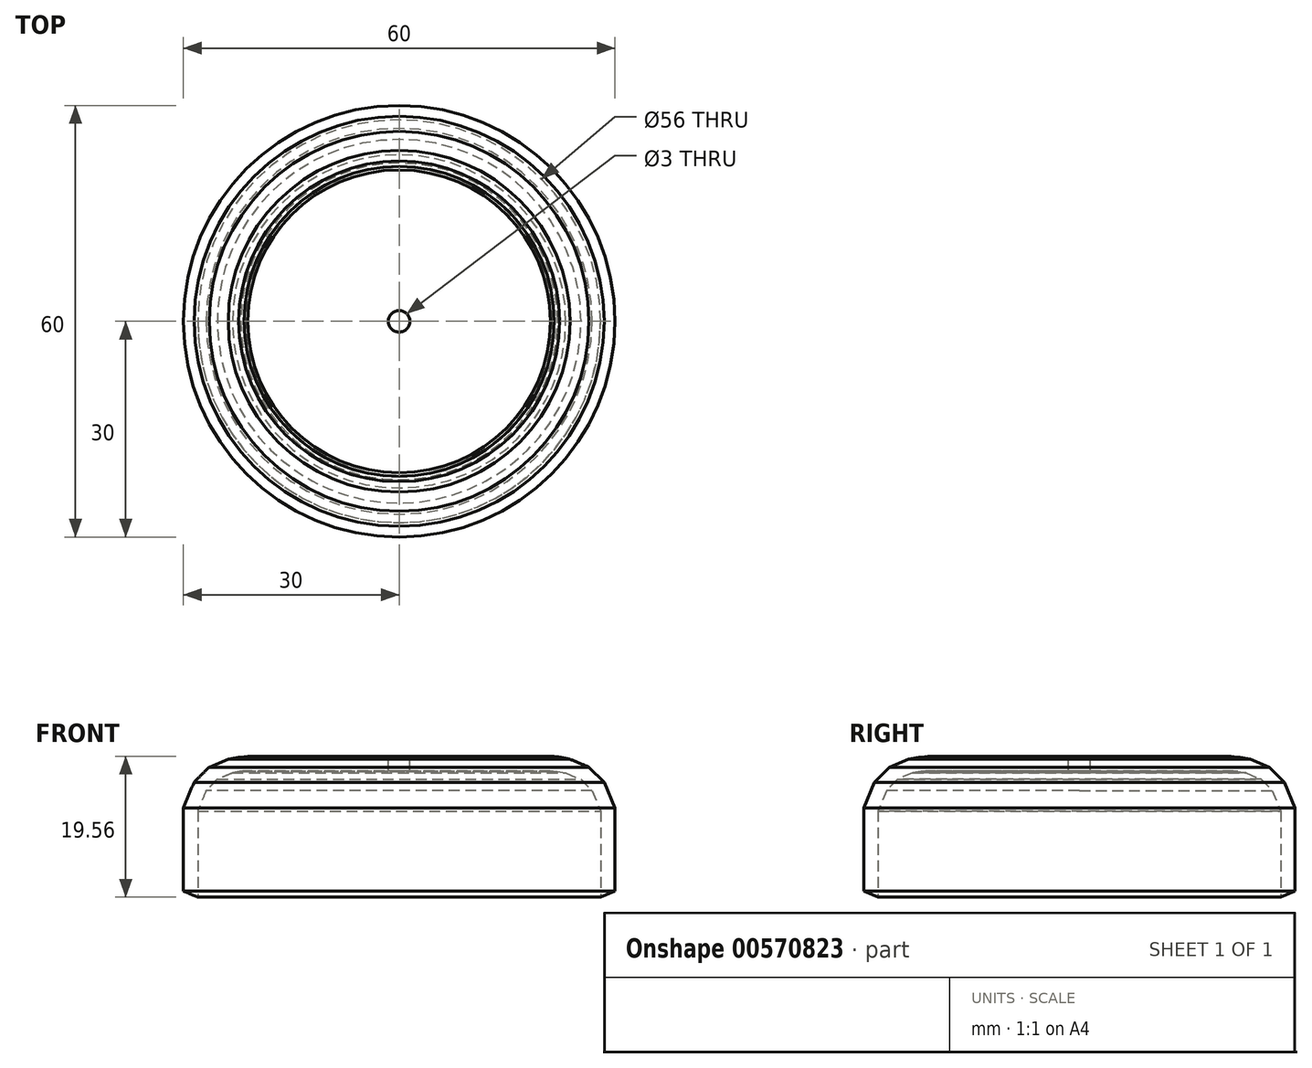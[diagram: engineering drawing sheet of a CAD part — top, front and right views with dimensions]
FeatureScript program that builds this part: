
annotation { "Feature Type Name" : "Feature", "Feature Type Description" : "" }
export const myFeature = defineFeature(function(context is Context, id is Id, definition is map)
    precondition{}
    {
        {
            var Q0;
            Q0=qCreatedBy(makeId("Top.planeOp"),FACE);
            var sketch = newSketch(context, id + "F0", { "sketchPlane" : qUnion([Q0])});
            skCircle(sketch, "E0", {"center": v(0, 0) * mm, "radius": 30 * mm});
            skSolve(sketch);
        }
        {
            var Q0;
            Q0=makeQuery(id+"F0.imprint","IMPRINT",FACE,{"disambiguationData":[TD([[makeQuery(id+"F0.imprint","IMPRINT",EDGE,{"derivedFrom":sQuery(id+"F0.wireOp",EDGE,"E0")}),1.0]])]});
            extrude(context, id + "F1", {"entities" : qUnion([Q0]), "depth" : 25.4 * mm, "offsetDistance" : 25.4 * mm});
        }
        {
            var Q0;
            Q0=makeQuery(id+"F1.opExtrude","CAP_EDGE",EDGE,{"disambiguationData":[OSD([sQuery(id+"F0.wireOp",EDGE,"E0")])],"isStart":false});
            chamfer(context, id + "F2", {"entities" : qUnion([Q0]), "width" : 5.08 * mm, "tangentPropagation" : true});
        }
        {
            var Q0;
            {var subQ0=sQuery(id+"F0.wireOp",EDGE,"E0");Q0=makeQuery(id+"F2.opChamfer","BLEND_EDGE",EDGE,{"blendedFrom":[makeQuery(id+"F1.opExtrude","CAP_EDGE",EDGE,{"disambiguationData":[OSD([subQ0])],"isStart":false}),makeQuery(id+"F1.opExtrude","CAP_FACE",FACE,{"disambiguationData":[OSD([subQ0])],"isStart":false})],"blendedInto":[makeQuery(id+"F1.opExtrude","CAP_FACE",FACE,{"disambiguationData":[OSD([subQ0])],"isStart":false})]});}
            chamfer(context, id + "F3", {"entities" : qUnion([Q0]), "width" : 5.08 * mm, "tangentPropagation" : true});
        }
        {
            var Q0;
            Q0=makeQuery(id+"F1.opExtrude","CAP_FACE",FACE,{"disambiguationData":[OSD([sQuery(id+"F0.wireOp",EDGE,"E0")])],"isStart":false});
            chamfer(context, id + "F4", {"entities" : qUnion([Q0]), "width" : 5.08 * mm, "tangentPropagation" : true});
        }
        {
            var Q0;
            {var subQ0=sQuery(id+"F0.wireOp",EDGE,"E0");var subQ1=makeQuery(id+"F1.opExtrude","CAP_FACE",FACE,{"disambiguationData":[OSD([subQ0])],"isStart":false});var subQ2=subQ1;Q0=makeQuery(id+"F4.opChamfer","BLEND_EDGE",EDGE,{"blendedFrom":[makeQuery(id+"F3.opChamfer","BLEND_EDGE",EDGE,{"blendedFrom":[makeQuery(id+"F2.opChamfer","BLEND_EDGE",EDGE,{"blendedFrom":[makeQuery(id+"F1.opExtrude","CAP_EDGE",EDGE,{"disambiguationData":[OSD([subQ0])],"isStart":false}),subQ1],"blendedInto":[subQ1]}),subQ2],"blendedInto":[subQ2]}),subQ2],"blendedInto":[subQ2]});}
            chamfer(context, id + "F5", {"entities" : qUnion([Q0]), "width" : 5.08 * mm, "tangentPropagation" : true});
        }
        {
            var Q0;
            {var subQ0=sQuery(id+"F0.wireOp",EDGE,"E0");Q0=makeQuery(id+"F2.opChamfer","BLEND_EDGE",EDGE,{"blendedFrom":[makeQuery(id+"F1.opExtrude","CAP_EDGE",EDGE,{"disambiguationData":[OSD([subQ0])],"isStart":false}),makeQuery(id+"F1.opExtrude","SWEPT_FACE",FACE,{"disambiguationData":[OSD([subQ0])]})],"blendedInto":[makeQuery(id+"F1.opExtrude","SWEPT_FACE",FACE,{"disambiguationData":[OSD([subQ0])]})]});}
            chamfer(context, id + "F6", {"entities" : qUnion([Q0]), "width" : 5.08 * mm, "tangentPropagation" : true});
        }
        {
            var Q0;
            {var subQ0=sQuery(id+"F0.wireOp",EDGE,"E0");var subQ1=makeQuery(id+"F1.opExtrude","CAP_FACE",FACE,{"disambiguationData":[OSD([subQ0])],"isStart":false});var subQ2=subQ1;var subQ3=subQ2;Q0=makeQuery(id+"F5.opChamfer","BLEND_EDGE",EDGE,{"blendedFrom":[makeQuery(id+"F4.opChamfer","BLEND_EDGE",EDGE,{"blendedFrom":[makeQuery(id+"F3.opChamfer","BLEND_EDGE",EDGE,{"blendedFrom":[makeQuery(id+"F2.opChamfer","BLEND_EDGE",EDGE,{"blendedFrom":[makeQuery(id+"F1.opExtrude","CAP_EDGE",EDGE,{"disambiguationData":[OSD([subQ0])],"isStart":false}),subQ1],"blendedInto":[subQ1]}),subQ2],"blendedInto":[subQ2]}),subQ3],"blendedInto":[subQ3]}),subQ3],"blendedInto":[subQ3]});}
            chamfer(context, id + "F7", {"entities" : qUnion([Q0]), "width" : 5.08 * mm, "tangentPropagation" : true});
        }
        {
            var Q0;
            Q0=makeQuery(id+"F1.opExtrude","CAP_FACE",FACE,{"disambiguationData":[OSD([sQuery(id+"F0.wireOp",EDGE,"E0")])],"isStart":true});
            shell(context, id + "F8", {"entities" : qUnion([Q0]), "thickness" : 2 * mm});
        }
        {
            var Q0;
            {var subQ0=sQuery(id+"F0.wireOp",EDGE,"E0");Q0=makeQuery(id+"F8.opShell","OFFSET_EDGE",EDGE,{"disambiguationData":[OSD([subQ0]),TDD([makeQuery(id+"F1.opExtrude","CAP_EDGE",EDGE,{"disambiguationData":[OSD([subQ0])],"isStart":true})])]});}
            chamfer(context, id + "F9", {"entities" : qUnion([Q0]), "width" : 2.54 * mm, "tangentPropagation" : true});
        }
        {
            var Q0;
            {var subQ0=sQuery(id+"F0.wireOp",EDGE,"E0");Q0=makeQuery(id+"F9.opChamfer","BLEND_EDGE",EDGE,{"blendedFrom":[makeQuery(id+"F8.opShell","OFFSET_EDGE",EDGE,{"disambiguationData":[OSD([subQ0]),TDD([makeQuery(id+"F1.opExtrude","CAP_EDGE",EDGE,{"disambiguationData":[OSD([subQ0])],"isStart":true})])]}),makeQuery(id+"F1.opExtrude","SWEPT_FACE",FACE,{"disambiguationData":[OSD([subQ0])]})],"blendedInto":[makeQuery(id+"F1.opExtrude","SWEPT_FACE",FACE,{"disambiguationData":[OSD([subQ0])]})]});}
            chamfer(context, id + "F10", {"entities" : qUnion([Q0]), "width" : 2.54 * mm, "tangentPropagation" : true});
        }
        {
            var Q0;
            Q0=makeQuery(id+"F1.opExtrude","CAP_FACE",FACE,{"disambiguationData":[OSD([sQuery(id+"F0.wireOp",EDGE,"E0")])],"isStart":false});
            var sketch = newSketch(context, id + "F11", { "sketchPlane" : qUnion([Q0])});
            skPoint(sketch, "E1", {"position": v(0, 0) * mm});
            skSolve(sketch);
        }
        {
            var Q0;
            Q0=sQuery(id+"F11.wireOp",VERTEX,"E1");
            var Q1;
            Q1=makeQuery(id+"F1.opExtrude","SWEPT_BODY",BODY,{"disambiguationData":[OSD([sQuery(id+"F0.wireOp",EDGE,"E0")])]});
            hole(context, id + "F12", {"style" : HoleStyle.SIMPLE, "endStyle" : HoleEndStyle.THROUGH, "holeDiameter" : 3 * mm, "majorDiameter" : 6.35 * mm, "isTappedThrough" : true, "tappedDepth" : 12.7 * mm, "tapClearance" : 3, "locations" : qUnion([Q0]), "scope" : qUnion([Q1])});
        }
    });
